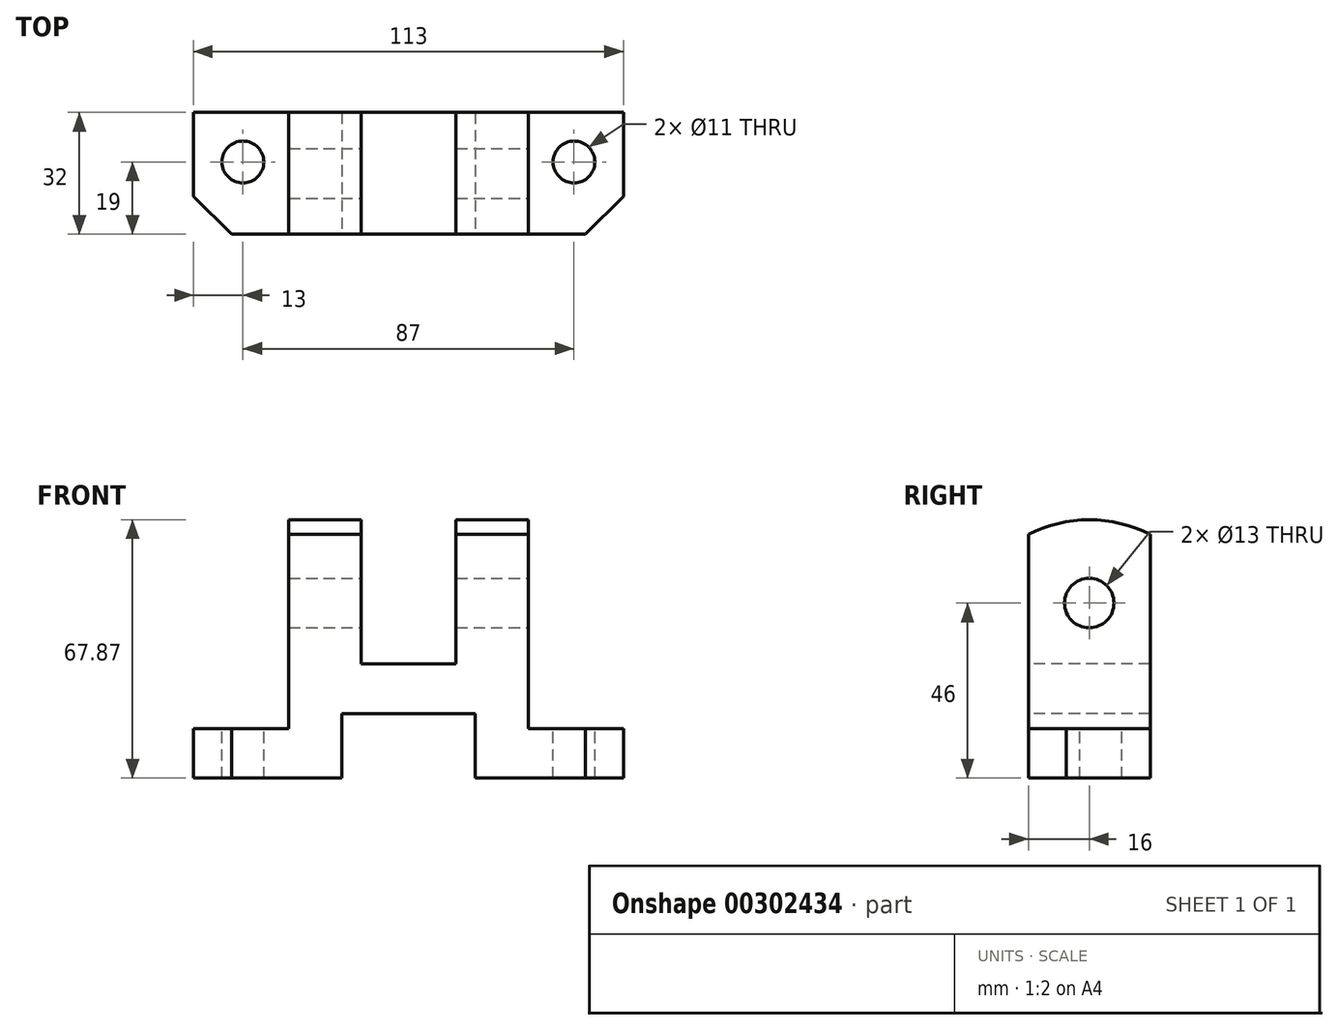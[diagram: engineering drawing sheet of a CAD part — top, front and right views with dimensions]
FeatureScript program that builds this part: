
annotation { "Feature Type Name" : "Feature", "Feature Type Description" : "" }
export const myFeature = defineFeature(function(context is Context, id is Id, definition is map)
    precondition{}
    {
        {
            var Q0;
            Q0=qCreatedBy(makeId("Front.planeOp"),FACE);
            var sketch = newSketch(context, id + "F0", { "sketchPlane" : qUnion([Q0])});
            skLineSegment(sketch, "E0", {"start": v(0, 0) * mm, "end": v(0, 13) * mm});
            skLineSegment(sketch, "E1", {"start": v(0, 13) * mm, "end": v(25, 13) * mm});
            skLineSegment(sketch, "E2", {"start": v(25, 13) * mm, "end": v(25, 64) * mm});
            skLineSegment(sketch, "E3", {"start": v(25, 64) * mm, "end": v(44, 64) * mm});
            skLineSegment(sketch, "E4", {"start": v(44, 64) * mm, "end": v(44, 30) * mm});
            skLineSegment(sketch, "E5", {"start": v(44, 30) * mm, "end": v(69, 30) * mm});
            skLineSegment(sketch, "E6", {"start": v(69, 30) * mm, "end": v(69, 64) * mm});
            skLineSegment(sketch, "E7", {"start": v(69, 64) * mm, "end": v(88, 64) * mm});
            skLineSegment(sketch, "E8", {"start": v(88, 64) * mm, "end": v(88, 13) * mm});
            skLineSegment(sketch, "E9", {"start": v(88, 13) * mm, "end": v(113, 13) * mm});
            skLineSegment(sketch, "E10", {"start": v(113, 13) * mm, "end": v(113, 0) * mm});
            skLineSegment(sketch, "E11", {"start": v(113, 0) * mm, "end": v(74, 0) * mm});
            skLineSegment(sketch, "E12", {"start": v(74, 0) * mm, "end": v(74, 17) * mm});
            skLineSegment(sketch, "E13", {"start": v(74, 17) * mm, "end": v(39, 17) * mm});
            skLineSegment(sketch, "E14", {"start": v(39, 17) * mm, "end": v(39, 0) * mm});
            skLineSegment(sketch, "E15", {"start": v(39, 0) * mm, "end": v(0, 0) * mm});
            skLineSegment(sketch, "E16", {"start": v(10, 13) * mm, "end": v(10, 0) * mm});
            skLineSegment(sketch, "E17", {"start": v(103, 13) * mm, "end": v(103, 0) * mm});
            skSolve(sketch);
        }
        {
            var Q0;
            Q0 = qSketchRegion(id + "F0", true);
            extrude(context, id + "F1", {"entities" : qUnion([Q0]), "oppositeDirection" : true, "depth" : 32 * mm});
        }
        {
            var Q0;
            Q0=makeQuery(id+"F1.opExtrude","SWEPT_FACE",FACE,{"disambiguationData":[OSD([sQuery(id+"F0.wireOp",EDGE,"E1")])]});
            var sketch = newSketch(context, id + "F2", { "sketchPlane" : qUnion([Q0])});
            skLineSegment(sketch, "E18", {"start": v(10, 0) * mm, "end": v(0, 10) * mm});
            skLineSegment(sketch, "E19", {"start": v(0, 10) * mm, "end": v(0, 0) * mm});
            skLineSegment(sketch, "E20", {"start": v(0, 0) * mm, "end": v(10, 0) * mm});
            skLineSegment(sketch, "E21", {"start": v(103, 0) * mm, "end": v(113, 0) * mm});
            skLineSegment(sketch, "E22", {"start": v(113, 0) * mm, "end": v(113, 10) * mm});
            skLineSegment(sketch, "E23", {"start": v(113, 10) * mm, "end": v(103, 0) * mm});
            skSolve(sketch);
        }
        {
            var Q0;
            Q0 = qSketchRegion(id + "F2", true);
            extrude(context, id + "F3", {"entities" : qUnion([Q0]), "operationType" : NewBodyOperationType.REMOVE, "oppositeDirection" : true, "depth" : 25 * mm});
        }
        {
            var Q0;
            Q0=makeQuery(id+"F1.opExtrude","SWEPT_FACE",FACE,{"disambiguationData":[OSD([sQuery(id+"F0.wireOp",EDGE,"E1")])]});
            var sketch = newSketch(context, id + "F4", { "sketchPlane" : qUnion([Q0])});
            skCircle(sketch, "E24", {"center": v(13, 19) * mm, "radius": 5.5 * mm});
            skCircle(sketch, "E25", {"center": v(100, 19) * mm, "radius": 5.5 * mm});
            skSolve(sketch);
        }
        {
            var Q0;
            Q0 = qSketchRegion(id + "F4", true);
            extrude(context, id + "F5", {"entities" : qUnion([Q0]), "operationType" : NewBodyOperationType.REMOVE, "endBound" : BoundingType.THROUGH_ALL, "oppositeDirection" : true, "depth" : 25 * mm});
        }
        {
            var Q0;
            Q0=makeQuery(id+"F1.opExtrude","SWEPT_FACE",FACE,{"disambiguationData":[OSD([sQuery(id+"F0.wireOp",EDGE,"E8")])]});
            var sketch = newSketch(context, id + "F6", { "sketchPlane" : qUnion([Q0])});
            skArc(sketch, "E26", {"start": v(32, 64) * mm, "mid": v(16, 67.87) * mm, "end": v(0, 64) * mm});
            skCircle(sketch, "E27", {"center": v(16, 46) * mm, "radius": 6.5 * mm});
            skSolve(sketch);
        }
        {
            var Q0;
            Q0=makeQuery(id+"F6.imprint","IMPRINT",FACE,{"disambiguationData":[TD([[makeQuery(id+"F6.imprint","IMPRINT",EDGE,{"derivedFrom":sQuery(id+"F6.wireOp",EDGE,"E27")}),1.0]])]});
            extrude(context, id + "F7", {"entities" : qUnion([Q0]), "operationType" : NewBodyOperationType.REMOVE, "endBound" : BoundingType.THROUGH_ALL, "oppositeDirection" : true, "depth" : 25 * mm});
        }
        {
            var Q0;
            Q0=makeQuery(id+"F6.imprint","IMPRINT",FACE,{"disambiguationData":[TD([[makeQuery(id+"F6.imprint","IMPRINT",EDGE,{"derivedFrom":sQuery(id+"F6.wireOp",EDGE,"E26")}),1.0]])]});
            extrude(context, id + "F8", {"entities" : qUnion([Q0]), "operationType" : NewBodyOperationType.ADD, "oppositeDirection" : true, "depth" : 19 * mm});
        }
        {
            var Q0;
            Q0=makeQuery(id+"F1.opExtrude","SWEPT_FACE",FACE,{"disambiguationData":[OSD([sQuery(id+"F0.wireOp",EDGE,"E2")])]});
            var sketch = newSketch(context, id + "F9", { "sketchPlane" : qUnion([Q0])});
            skArc(sketch, "E28", {"start": v(0, 64) * mm, "mid": v(-16, 67.87) * mm, "end": v(-32, 64) * mm});
            skSolve(sketch);
        }
        {
            var Q0;
            Q0=makeQuery(id+"F9.imprint","IMPRINT",FACE,{"disambiguationData":[TD([[makeQuery(id+"F9.imprint","IMPRINT",EDGE,{"derivedFrom":sQuery(id+"F9.wireOp",EDGE,"E28")}),1.0]])]});
            extrude(context, id + "F10", {"entities" : qUnion([Q0]), "operationType" : NewBodyOperationType.ADD, "oppositeDirection" : true, "depth" : 19 * mm});
        }
    });
